# Revit family: Hager-FW-Hollow_wall-IP30-With_Cover-With_DIN-Hosted-AT-de
name_source: partatom
category: Electrical Equipment
units: mm (PartAtom-declared; Revit-internal decimal feet)

## family parameters
Cut with Voids When Loaded = No
Host = Face
Maintain Annotation Orientation = Yes
Panel Configuration = Two Columns, Circuits Across
Part Type = Panelboard
Room Calculation Point = No
Round Connector Dimension = Use Diameter
Shared = No

## types (7) — shared parameters
BC_MODEL_ID = 1554214
BC_OBJECT_ID = 513828
BC_OBJECT_VERSION = #3
Code hager = ADD-EC000214_EU
EF000003 - Montageart = Hohlwand
EF000007 - Farbe = weiß
EF000008 - Breite = 603 mm
EF000024 - UV-beständig = No
EF000049 - Tiefe = 125 mm  [stored 0.410105 ft]
EF000116 - RAL-Nummer = 9010
EF000218 - Einbautiefe = 112 mm  [stored 0.367454 ft]
EF000846 - Einbaubreite = 560 mm  [stored 1.83727 ft]
EF001062 - EMV-Ausführung = No
EF001088 - Anbaumöglichkeit = Yes
EF001134 - DIN-Schiene = Yes
EF004462 - Art der Schließung = sonstige
EF005474 - Schutzart (IP) = IP30
EF006244 - Transparenter Deckel/Tür = No
EF006306 - Mit Schloss = No
ETIM class code = EC000214
ETIM class name = Small distribution board
HG000001-Anzahl der Spalten = 1
HG000002-Mit tür = Yes
HG000003-Bereich = FW
HG000005-Dicke = 2 mm  [stored 0.00656168 ft]
HG000006-Unterputz = Yes
HG000009-Doppelflügeligen Tür = No
HG000010-Asymmetrische Türen = No
HG000011-Leere Reihen von unten = No
HG000012-Türschwenkwinkel = 90.00°
HG000013-Tür links = No
HG000014-Tür rechts = Yes
HG000015-Sichtbarkeit der Türöffnung = Yes
HG000016-3D-Türsichtbarkeit = Yes
HG000017-Distanz zwischen den Polen = 18 mm  [stored 0.0590551 ft]
HG000060-RAL-number = 9010
HG000099-Onfly Template ID-de-AT = 507532
Manufacturer = Hager
Name = FW-Hollow_wall-IP30-With_Cover-With_DIN-AT
Name BIM&CO = Electricity
Name hager = ADD_Enclosures_EC000214
Uniformat = Low Tension Service & Dist.
Uniformat code = D501001
zero-valued in all types: Default Elevation, EF001131 - Innentiefe

## per-type parameters (varying)
| type | BC_VARIANT_ID | EF000040 - Höhe | EF000118 - Mit Montageplatte | EF000266 - Anzahl der Reihen | EF000332 - Einbauhöhe | EF002950 - Breite in Teilungseinheiten | EF009212 - Ausführung Deckel | EF015776 - Erdungsklemmenblock | EF015777 - Neutralleiterklemmenblock | EF015941 - Signaldurchlassende Tür | HG000004-Herstellerreferenz | HG000007-Anzahl der leeren Spalten | HG000008-Anzahl der leeren Reihen | HGEF000266-Anzahl der Reihen | HGEF0002950-Breite in Teilungseinheiten |
| FW-Hollow_wall_W603_H703_D125_24_Modular_Spacing-FWU42K3 | 1178604 | 703 mm  [stored 2.30643 ft] | Yes | 4 | 652 mm  [stored 2.13911 ft] | 24 | mit Ausschnitt | Yes | Yes | Yes | FWU42K3 | 1 | 4 | 4 | 24 |
| FW-Hollow_wall_W603_H703_D125_26_Modular_Spacing-FWU42M2 | 1178606 | 703 mm  [stored 2.30643 ft] | No | 4 | 652 mm  [stored 2.13911 ft] | 26 | mit Ausschnitt | No | No | No | FWU42M2 | 0 | 0 | 4 | 26 |
| FW-Hollow_wall_W603_H853_D125_24_Modular_Spacing-FWU52K3 | 1178607 | 853 mm  [stored 2.79856 ft] | Yes | 5 | 802 mm  [stored 2.63123 ft] | 24 | mit Ausschnitt | Yes | Yes | Yes | FWU52K3 | 1 | 5 | 5 | 24 |
| FW-Hollow_wall_W603_H853_D125_26_Modular_Spacing-FWU52M2 | 1178608 | 853 mm  [stored 2.79856 ft] | No | 5 | 802 mm  [stored 2.63123 ft] | 26 | mit Ausschnitt | No | No | No | FWU52M2 | 0 | 0 | 5 | 26 |
| FW-Hollow_wall_W603_H1003_D125_24_Modular_Spacing-FWU62K3 | 1178609 | 1003 mm  [stored 3.29068 ft] | Yes | 6 | 952 mm  [stored 3.12336 ft] | 24 | geschlossen | Yes | Yes | Yes | FWU62K3 | 1 | 6 | 6 | 24 |
| FW-Hollow_wall_W603_H1003_D125_26_Modular_Spacing-FWU62M2 | 1178610 | 1003 mm  [stored 3.29068 ft] | No | 6 | 952 mm  [stored 3.12336 ft] | 26 | mit Ausschnitt | No | No | No | FWU62M2 | 0 | 0 | 6 | 26 |
| FW-Hollow_wall_W603_H1153_D125_26_Modular_Spacing-FWU72M2 | 1178611 | 1153 mm | No | 7 | 1102 mm  [stored 3.61549 ft] | 26 | mit Ausschnitt | No | No | No | FWU72M2 | 0 | 0 | 7 | 26 |

note: column(s) folded — value = type name in every type: Reference

note: [stored X ft] marks values corroborated as IEEE doubles in the binary element streams (Revit-internal decimal feet)

## geometry (parser evidence)
native form markers: Sweep x16
no freeform markers — native parametric forms only
